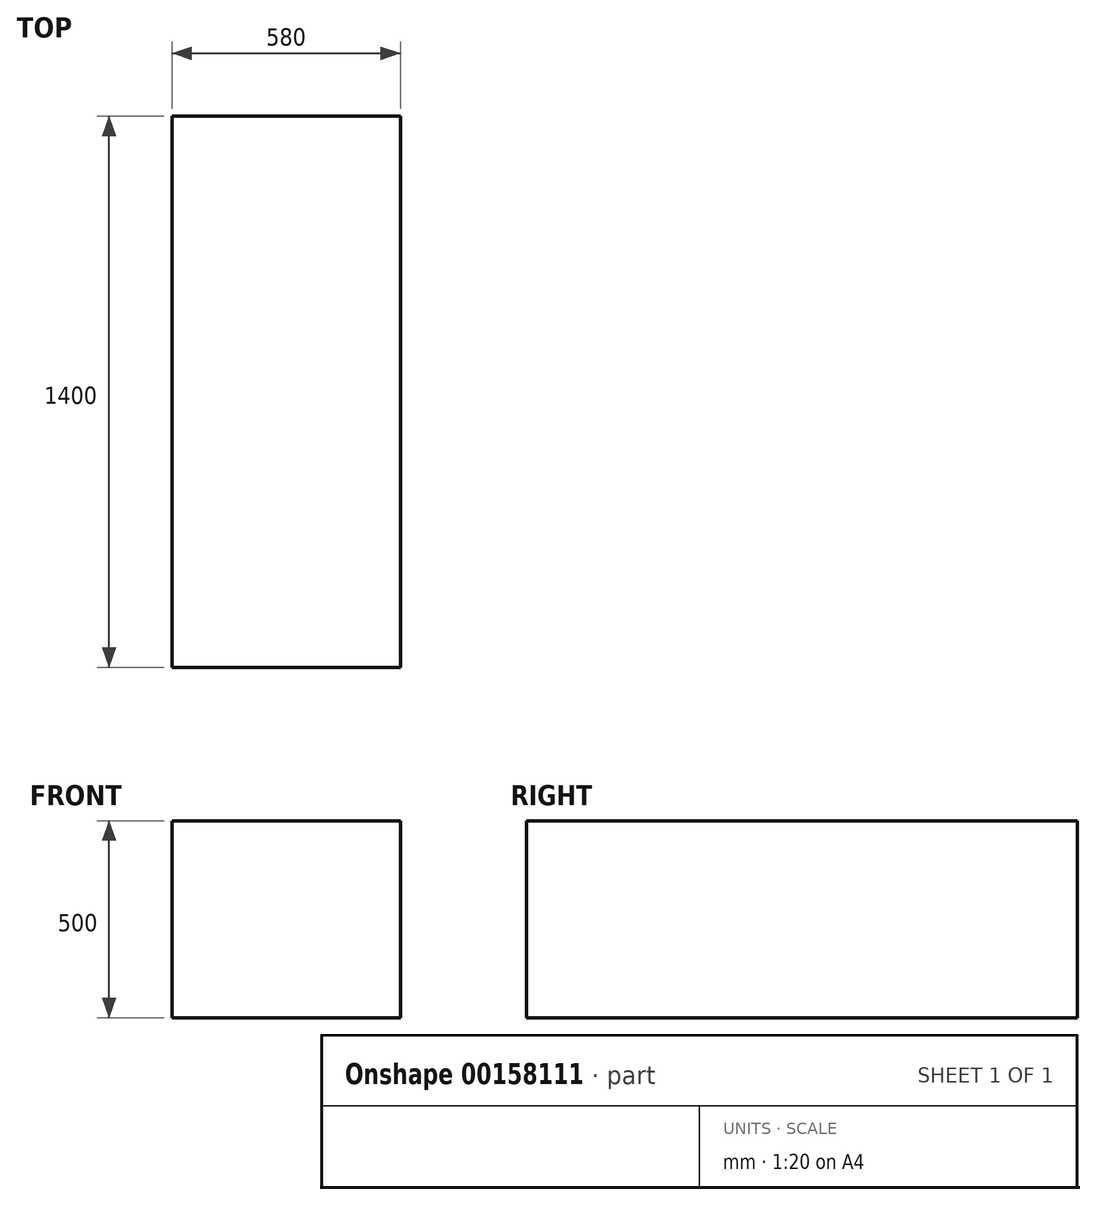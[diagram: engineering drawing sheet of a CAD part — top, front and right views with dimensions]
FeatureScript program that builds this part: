
annotation { "Feature Type Name" : "Feature", "Feature Type Description" : "" }
export const myFeature = defineFeature(function(context is Context, id is Id, definition is map)
    precondition{}
    {
        {
            var Q0;
            Q0=qCreatedBy(makeId("Front.planeOp"),FACE);
            var sketch = newSketch(context, id + "F0", { "sketchPlane" : qUnion([Q0])});
            skLineSegment(sketch, "E0.bottom", {"start": v(290, 250) * mm, "end": v(-290, 250) * mm});
            skLineSegment(sketch, "E0.top", {"start": v(290, -250) * mm, "end": v(-290, -250) * mm});
            skLineSegment(sketch, "E0.left", {"start": v(290, 250) * mm, "end": v(290, -250) * mm});
            skLineSegment(sketch, "E0.right", {"start": v(-290, 250) * mm, "end": v(-290, -250) * mm});
            skPoint(sketch, "E0.middle", {"position": v(0, 0) * mm});
            skSolve(sketch);
        }
        {
            var Q0;
            Q0 = qSketchRegion(id + "F0", true);
            extrude(context, id + "F1", {"entities" : qUnion([Q0]), "depth" : 1400 * mm});
        }
    });
